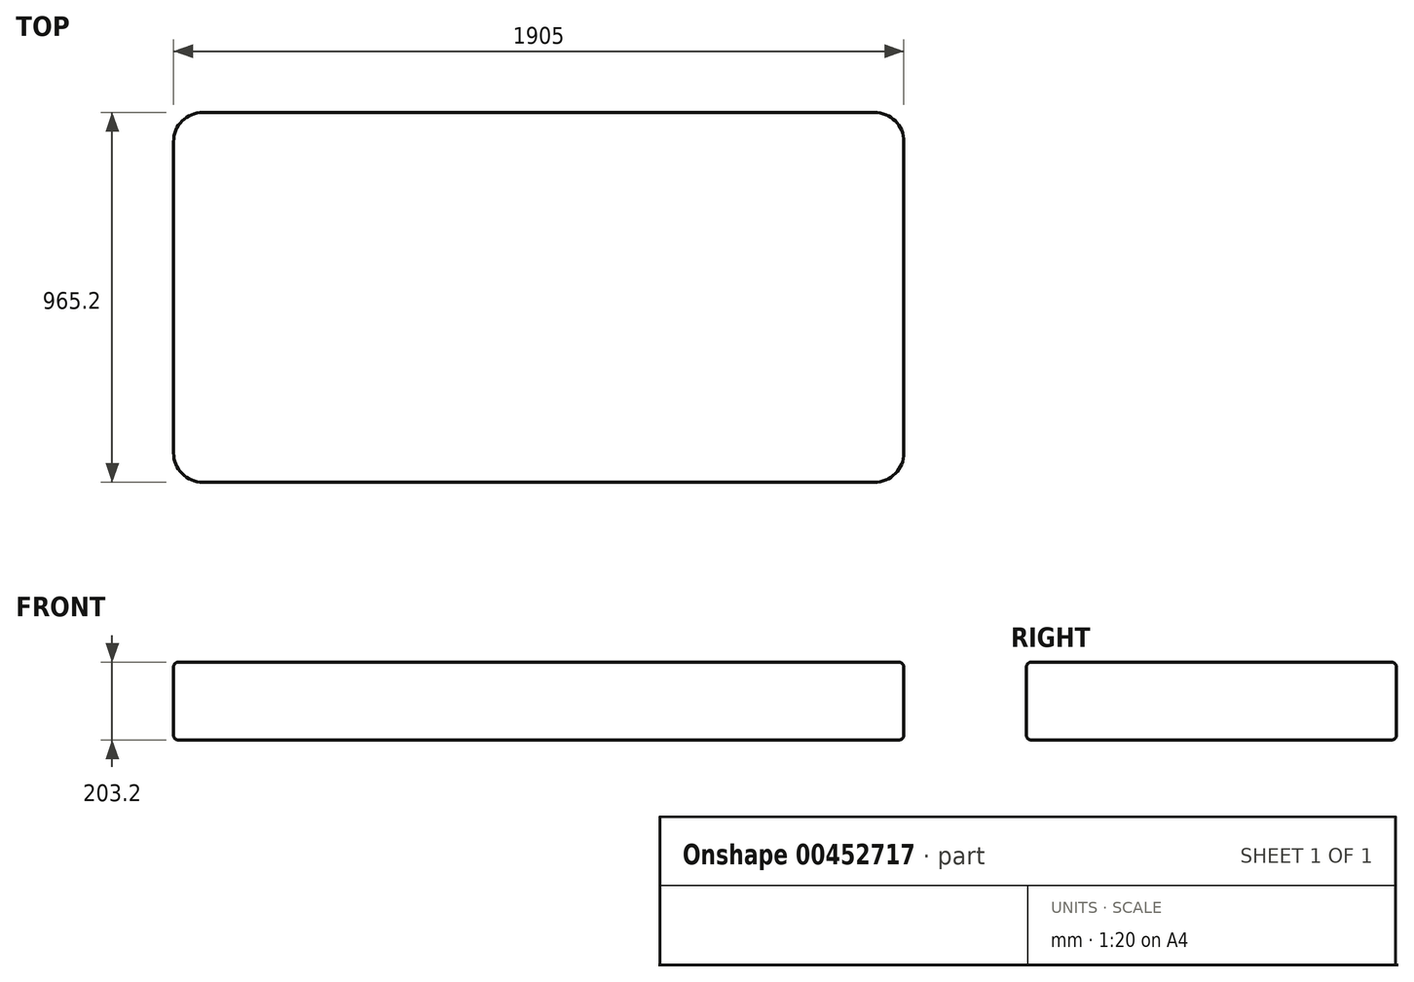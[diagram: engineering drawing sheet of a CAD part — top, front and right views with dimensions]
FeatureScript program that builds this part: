
annotation { "Feature Type Name" : "Feature", "Feature Type Description" : "" }
export const myFeature = defineFeature(function(context is Context, id is Id, definition is map)
    precondition{}
    {
        {
            var Q0;
            Q0=qCreatedBy(makeId("Top.planeOp"),FACE);
            var sketch = newSketch(context, id + "F0", { "sketchPlane" : qUnion([Q0])});
            skLineSegment(sketch, "E0.bottom", {"start": v(952.5, 482.6) * mm, "end": v(-952.5, 482.6) * mm});
            skLineSegment(sketch, "E0.top", {"start": v(952.5, -482.6) * mm, "end": v(-952.5, -482.6) * mm});
            skLineSegment(sketch, "E0.left", {"start": v(952.5, 482.6) * mm, "end": v(952.5, -482.6) * mm});
            skLineSegment(sketch, "E0.right", {"start": v(-952.5, 482.6) * mm, "end": v(-952.5, -482.6) * mm});
            skPoint(sketch, "E0.middle", {"position": v(0, 0) * mm});
            skSolve(sketch);
        }
        {
            var Q0;
            Q0 = qSketchRegion(id + "F0", true);
            extrude(context, id + "F1", {"entities" : qUnion([Q0]), "depth" : 203.2 * mm});
        }
        {
            var Q0;
            Q0=makeQuery(id+"F1.opExtrude","SWEPT_EDGE",EDGE,{"disambiguationData":[OSD([sQuery(id+"F0.wireOp",EDGE,"E0.top"),sQuery(id+"F0.wireOp",EDGE,"E0.right")])]});
            var Q1;
            Q1=makeQuery(id+"F1.opExtrude","SWEPT_EDGE",EDGE,{"disambiguationData":[OSD([sQuery(id+"F0.wireOp",EDGE,"E0.top"),sQuery(id+"F0.wireOp",EDGE,"E0.left")])]});
            var Q2;
            Q2=makeQuery(id+"F1.opExtrude","SWEPT_EDGE",EDGE,{"disambiguationData":[OSD([sQuery(id+"F0.wireOp",EDGE,"E0.bottom"),sQuery(id+"F0.wireOp",EDGE,"E0.left")])]});
            var Q3;
            Q3=makeQuery(id+"F1.opExtrude","SWEPT_EDGE",EDGE,{"disambiguationData":[OSD([sQuery(id+"F0.wireOp",EDGE,"E0.bottom"),sQuery(id+"F0.wireOp",EDGE,"E0.right")])]});
            fillet(context, id + "F2", {"entities" : qUnion([Q0, Q1, Q2, Q3]), "radius" : 76.2 * mm, "tangentPropagation" : true, "allowEdgeOverflow" : false});
        }
        {
            var Q0;
            Q0=makeQuery(id+"F1.opExtrude","CAP_EDGE",EDGE,{"disambiguationData":[OSD([sQuery(id+"F0.wireOp",EDGE,"E0.top")])],"isStart":false});
            var Q1;
            Q1=makeQuery(id+"F1.opExtrude","CAP_EDGE",EDGE,{"disambiguationData":[OSD([sQuery(id+"F0.wireOp",EDGE,"E0.top")])],"isStart":true});
            fillet(context, id + "F3", {"entities" : qUnion([Q0, Q1]), "radius" : 12.7 * mm, "tangentPropagation" : true, "allowEdgeOverflow" : false});
        }
    });
